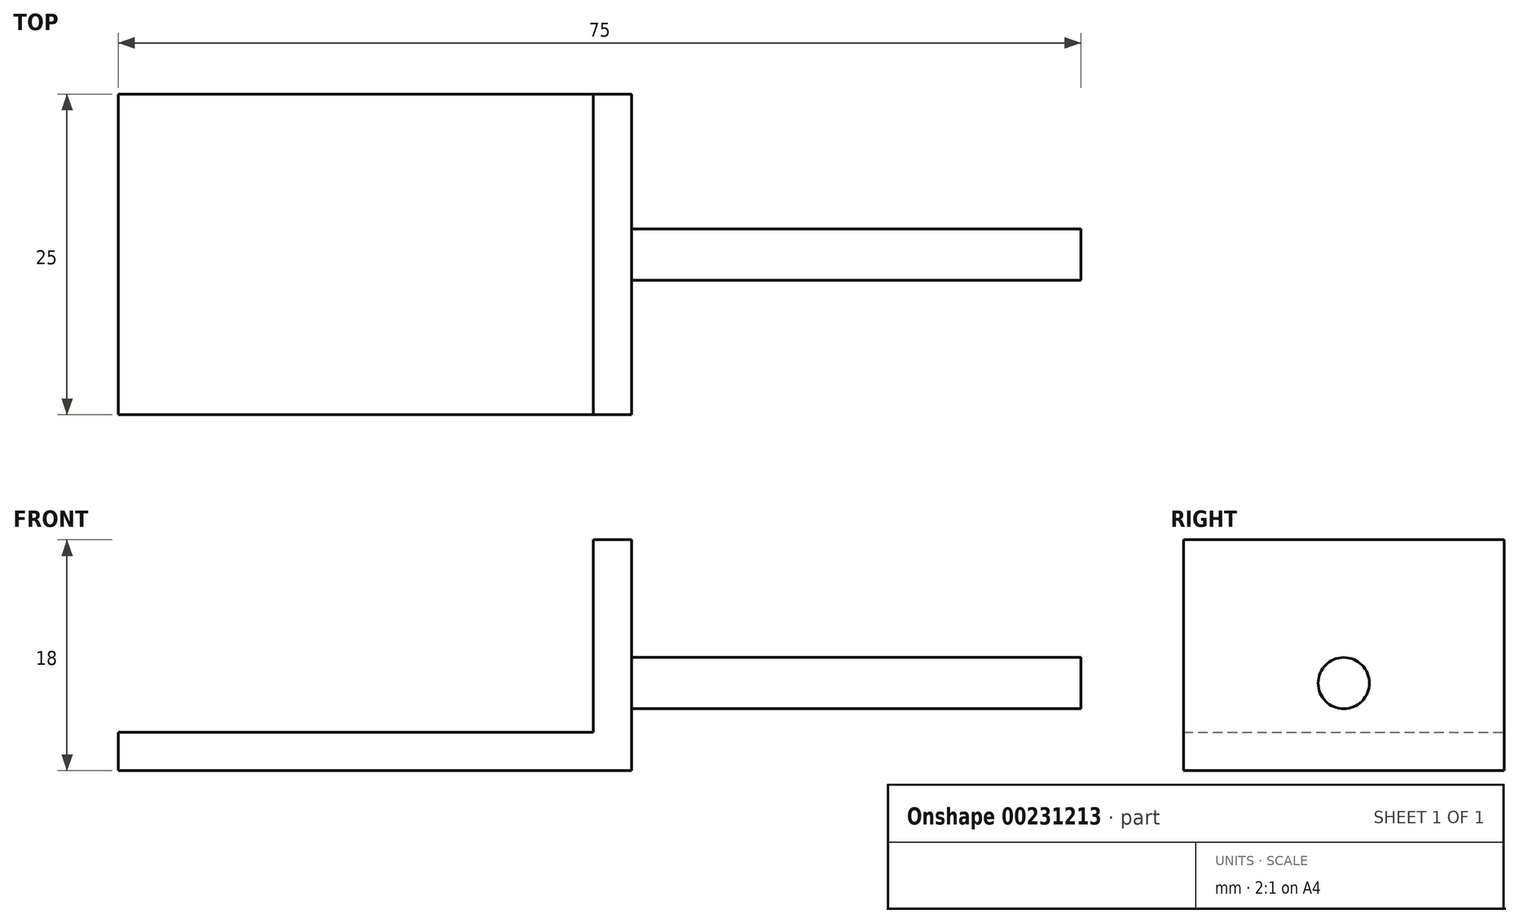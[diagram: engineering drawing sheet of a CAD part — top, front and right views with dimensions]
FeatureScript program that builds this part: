
annotation { "Feature Type Name" : "Feature", "Feature Type Description" : "" }
export const myFeature = defineFeature(function(context is Context, id is Id, definition is map)
    precondition{}
    {
        {
            var Q0;
            Q0=qCreatedBy(makeId("Front.planeOp"),FACE);
            var sketch = newSketch(context, id + "F0", { "sketchPlane" : qUnion([Q0])});
            skLineSegment(sketch, "E0", {"start": v(-37, 0) * mm, "end": v(0, 0) * mm});
            skLineSegment(sketch, "E1", {"start": v(0, 0) * mm, "end": v(0, 15) * mm});
            skLineSegment(sketch, "E2", {"start": v(0, 15) * mm, "end": v(3, 15) * mm});
            skLineSegment(sketch, "E3", {"start": v(3, 15) * mm, "end": v(3, -3) * mm});
            skLineSegment(sketch, "E4", {"start": v(3, -3) * mm, "end": v(-37, -3) * mm});
            skLineSegment(sketch, "E5", {"start": v(-37, -3) * mm, "end": v(-37, 0) * mm});
            skSolve(sketch);
        }
        {
            var Q0;
            Q0=qCreatedBy(makeId("Front.planeOp"),FACE);
            var sketch = newSketch(context, id + "F1", { "sketchPlane" : qUnion([Q0])});
            skLineSegment(sketch, "E6", {"start": v(3, 3.82) * mm, "end": v(38, 3.82) * mm});
            skLineSegment(sketch, "E7", {"start": v(38, 3.82) * mm, "end": v(38, 1.82) * mm});
            skLineSegment(sketch, "E8", {"start": v(38, 1.82) * mm, "end": v(3, 1.82) * mm});
            skLineSegment(sketch, "E9", {"start": v(3, 3.82) * mm, "end": v(3, 1.82) * mm});
            skSolve(sketch);
        }
        {
            var Q0;
            Q0 = qSketchRegion(id + "F0", true);
            extrude(context, id + "F2", {"entities" : qUnion([Q0]), "endBound" : BoundingType.SYMMETRIC, "depth" : 25 * mm});
        }
        {
            var Q0;
            Q0 = qSketchRegion(id + "F1", true);
            var Q1;
            Q1=sQuery(id+"F1.wireOp",EDGE,"E6");
            revolve(context, id + "F3", {"operationType" : NewBodyOperationType.ADD, "entities" : qUnion([Q0]), "axis" : qUnion([Q1]), "revolveType" : RevolveType.FULL});
        }
    });
